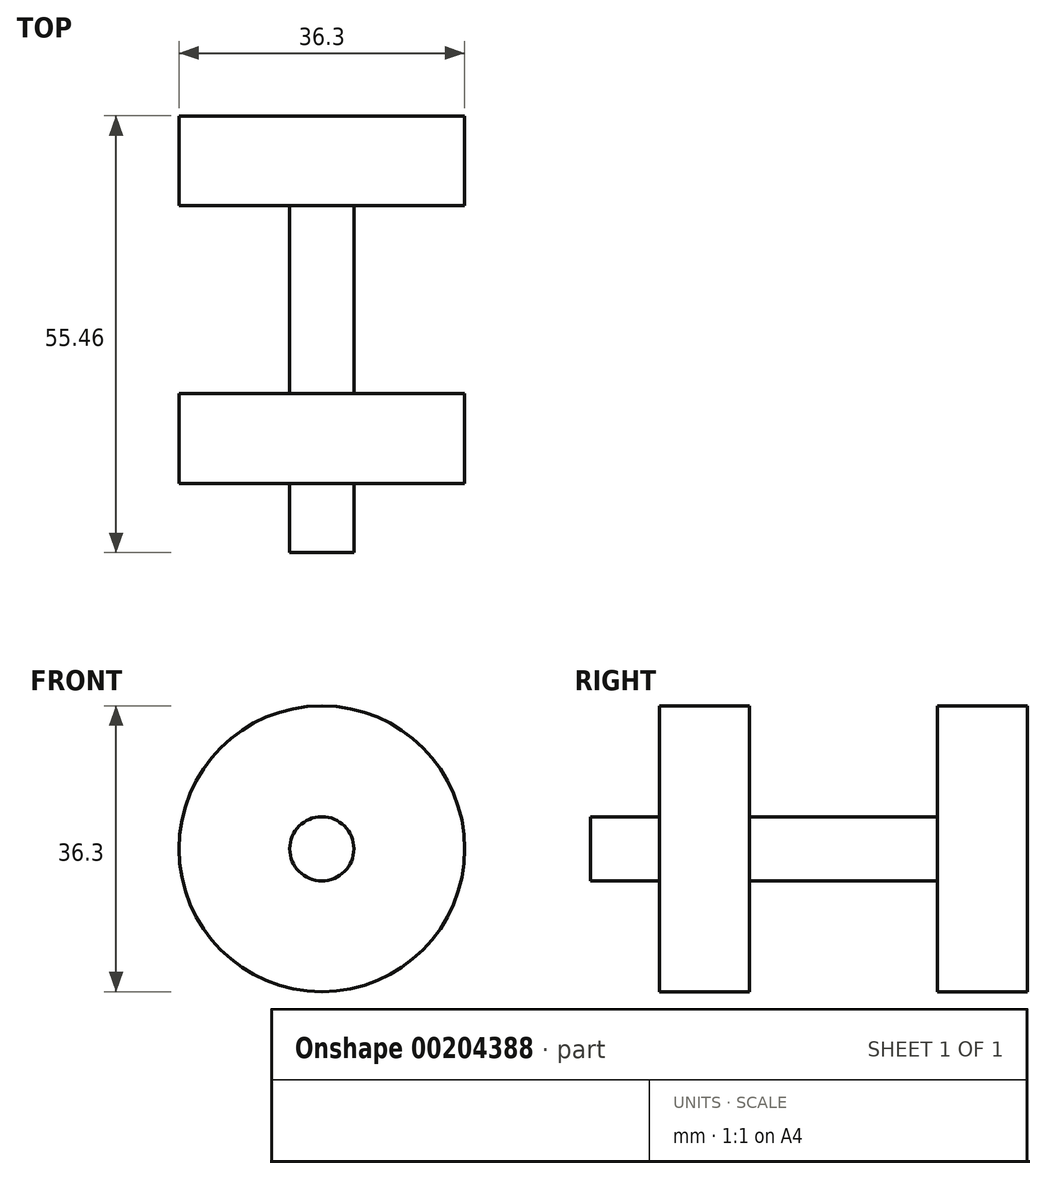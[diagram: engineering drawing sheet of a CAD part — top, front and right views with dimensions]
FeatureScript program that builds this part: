
annotation { "Feature Type Name" : "Feature", "Feature Type Description" : "" }
export const myFeature = defineFeature(function(context is Context, id is Id, definition is map)
    precondition{}
    {
        {
            var Q0;
            Q0=qCreatedBy(makeId("Right.planeOp"),FACE);
            var sketch = newSketch(context, id + "F0", { "sketchPlane" : qUnion([Q0])});
            skLineSegment(sketch, "E0.bottom", {"start": v(-27.72, 4.08) * mm, "end": v(27.74, 4.08) * mm});
            skLineSegment(sketch, "E0.top", {"start": v(-27.72, -5.1) * mm, "end": v(27.74, -5.1) * mm});
            skLineSegment(sketch, "E0.left", {"start": v(-27.72, 4.08) * mm, "end": v(-27.72, -5.1) * mm});
            skLineSegment(sketch, "E0.right", {"start": v(27.74, 4.08) * mm, "end": v(27.74, -5.1) * mm});
            skLineSegment(sketch, "E1.bottom", {"start": v(-18.95, -5.1) * mm, "end": v(-7.53, -5.1) * mm});
            skLineSegment(sketch, "E1.top", {"start": v(-18.95, 18.15) * mm, "end": v(-7.53, 18.15) * mm});
            skLineSegment(sketch, "E2.bottom", {"start": v(27.74, -5.1) * mm, "end": v(16.32, -5.1) * mm});
            skLineSegment(sketch, "E2.top", {"start": v(27.74, 18.15) * mm, "end": v(16.32, 18.15) * mm});
            skLineSegment(sketch, "E3", {"start": v(-36.49, 0) * mm, "end": v(39.77, 0) * mm});
            skLineSegment(sketch, "E4", {"start": v(-18.95, 18.15) * mm, "end": v(-18.95, 4.08) * mm});
            skLineSegment(sketch, "E5", {"start": v(-7.53, 18.15) * mm, "end": v(-7.53, 4.08) * mm});
            skLineSegment(sketch, "E6", {"start": v(16.32, 18.15) * mm, "end": v(16.32, 4.08) * mm});
            skLineSegment(sketch, "E7", {"start": v(27.74, 18.15) * mm, "end": v(27.74, 4.08) * mm});
            skSolve(sketch);
        }
        {
            var Q0;
            Q0=makeQuery(id+"F0.imprint","IMPRINT",FACE,{"disambiguationData":[TD([[makeQuery(id+"F0.imprint","IMPRINT",EDGE,{"derivedFrom":sQuery(id+"F0.wireOp",EDGE,"E1.top")}),-1.0]])]});
            var Q1;
            Q1=makeQuery(id+"F0.imprint","IMPRINT",FACE,{"disambiguationData":[TD([[makeQuery(id+"F0.imprint","IMPRINT",EDGE,{"derivedFrom":sQuery(id+"F0.wireOp",EDGE,"E2.top")}),1.0]])]});
            var Q2;
            {var subQ1=sQuery(id+"F0.wireOp",EDGE,"E0.bottom");var subQ8=sQuery(id+"F0.wireOp",EDGE,"E0.left");var subQ9=makeQuery(id+"F0.imprint","INTERSECT",VERTEX,{"derivedFrom":[subQ1,subQ8]});Q2=makeQuery(id+"F0.imprint","IMPRINT",FACE,{"disambiguationData":[TD([[makeQuery(id+"F0.imprint","IMPRINT",EDGE,{"disambiguationData":[TD([[subQ9,-1.0]])],"derivedFrom":subQ1}),-1.0]])]});}
            var Q3;
            Q3=sQuery(id+"F0.wireOp",EDGE,"E3");
            revolve(context, id + "F1", {"entities" : qUnion([Q0, Q1, Q2]), "axis" : qUnion([Q3]), "revolveType" : RevolveType.FULL});
        }
    });
